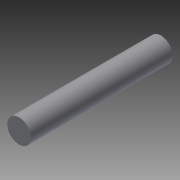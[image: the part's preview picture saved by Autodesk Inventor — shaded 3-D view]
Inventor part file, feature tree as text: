
AUTODESK INVENTOR PART (.ipt)
format: ipt  version: 2014 SP1 (Build 180222100, 222)  size: 69,632 bytes
history: native  units: in
note: dims shown in document units (in); Inventor stores cm internally (conversion verified against a paired STEP export)
features: extrude x1, sketch x1
ambient origin geometry x8: Origin, YZ Plane, XZ Plane, XY Plane, X Axis, Y Axis, Z Axis, Center Point
bodies: Solid1 (feature_tree)
feature tree (2):
  extrude  "Extrusion1"  Depth=1.5in TaperAngle=0.0deg
  sketch  "Sketch1"  dims[d0=0.25in d1=1.5in d2=0.0in]
